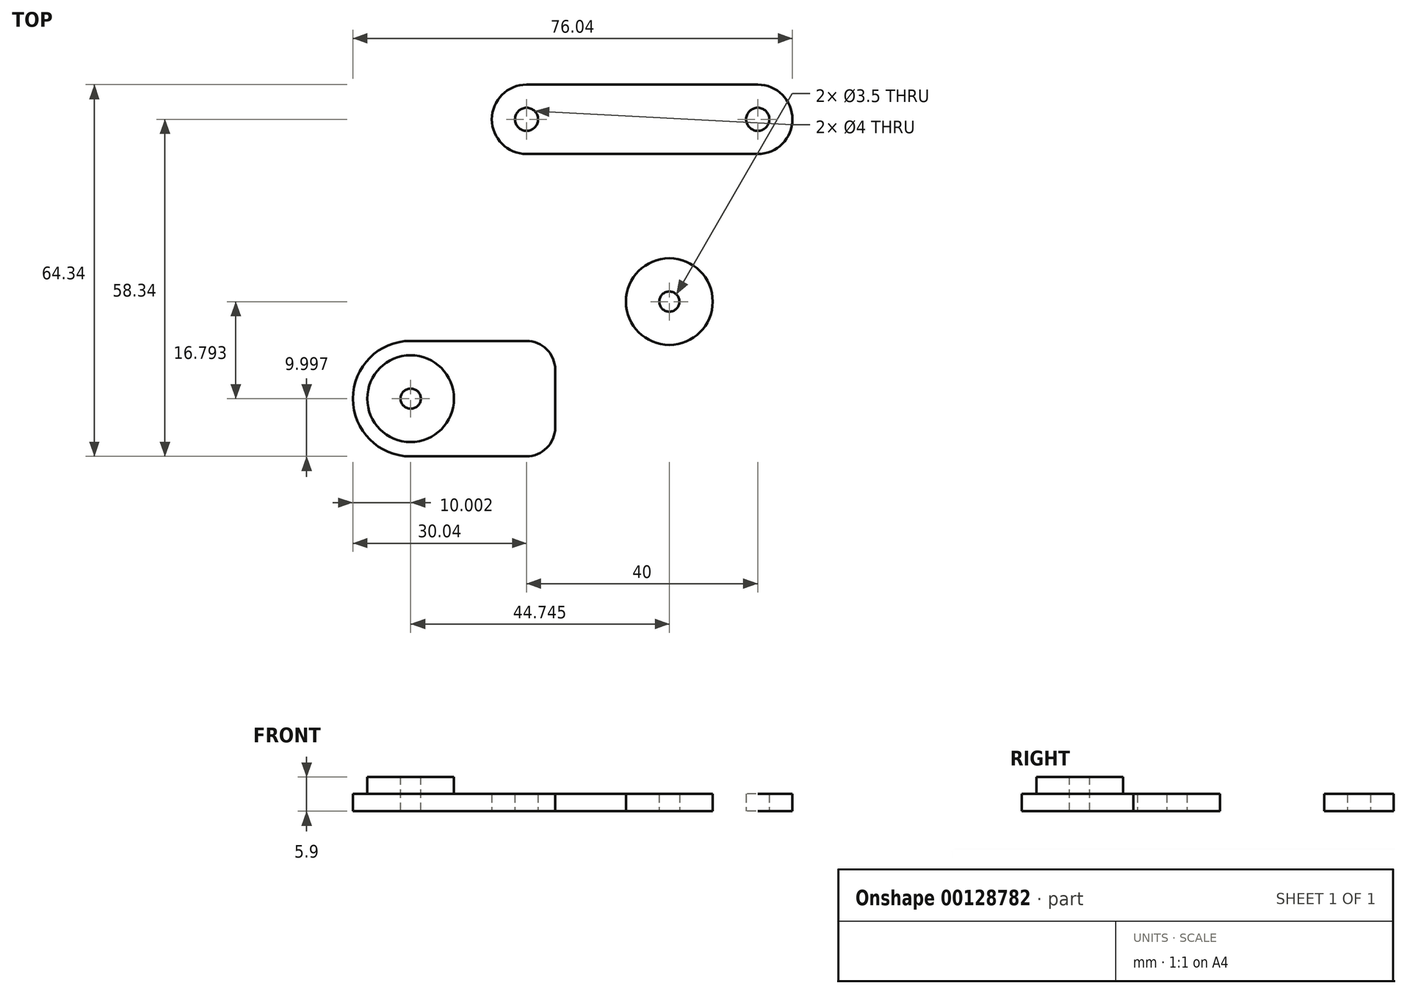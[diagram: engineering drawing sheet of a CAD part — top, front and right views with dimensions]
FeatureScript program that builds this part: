
annotation { "Feature Type Name" : "Feature", "Feature Type Description" : "" }
export const myFeature = defineFeature(function(context is Context, id is Id, definition is map)
    precondition{}
    {
        {
            var Q0;
            Q0=qCreatedBy(makeId("Top.planeOp"),FACE);
            var sketch = newSketch(context, id + "F0", { "sketchPlane" : qUnion([Q0])});
            skCircle(sketch, "E0", {"center": v(0, 0) * mm, "radius": 6 * mm});
            skCircle(sketch, "E1", {"center": v(-40, 0) * mm, "radius": 6 * mm});
            skLineSegment(sketch, "E2", {"start": v(-40, 6) * mm, "end": v(0, 6) * mm});
            skLineSegment(sketch, "E3", {"start": v(0, -6) * mm, "end": v(-40, -6) * mm});
            skCircle(sketch, "E4", {"center": v(-40, 0) * mm, "radius": 2 * mm});
            skCircle(sketch, "E5", {"center": v(0, 0) * mm, "radius": 2 * mm});
            skSolve(sketch);
        }
        {
            var Q0;
            Q0 = qSketchRegion(id + "F0", true);
            extrude(context, id + "F1", {"entities" : qUnion([Q0]), "depth" : 3 * mm});
        }
        {
            var Q0;
            Q0=qCreatedBy(makeId("Top.planeOp"),FACE);
            var sketch = newSketch(context, id + "F2", { "sketchPlane" : qUnion([Q0])});
            skLineSegment(sketch, "E6.bottom", {"start": v(-60.04, -38.34) * mm, "end": v(-35.04, -38.34) * mm});
            skLineSegment(sketch, "E6.top", {"start": v(-60.04, -58.34) * mm, "end": v(-35.04, -58.34) * mm});
            skLineSegment(sketch, "E6.right", {"start": v(-35.04, -38.34) * mm, "end": v(-35.04, -58.34) * mm});
            skArc(sketch, "E7", {"start": v(-60.04, -38.34) * mm, "mid": v(-70.04, -48.34) * mm, "end": v(-60.04, -58.34) * mm});
            skSolve(sketch);
        }
        {
            var Q0;
            Q0 = qSketchRegion(id + "F2", true);
            var Q1;
            Q1 = qConstructionFilter(qBodyType(qCreatedBy(id + "F2" ,EDGE), BodyType.WIRE), ConstructionObject.NO);
            extrude(context, id + "F3", {"entities" : qUnion([Q0]), "surfaceEntities" : qUnion([Q1]), "depth" : 3 * mm});
        }
        {
            var Q0;
            Q0=makeQuery(id+"F3.opExtrude","CAP_FACE",FACE,{"disambiguationData":[OSD([sQuery(id+"F2.wireOp",EDGE,"E6.bottom"),sQuery(id+"F2.wireOp",EDGE,"E6.top"),sQuery(id+"F2.wireOp",EDGE,"E6.right"),sQuery(id+"F2.wireOp",EDGE,"E7")])],"isStart":false});
            var sketch = newSketch(context, id + "F4", { "sketchPlane" : qUnion([Q0])});
            skCircle(sketch, "E8", {"center": v(-60.04, -48.34) * mm, "radius": 7.5 * mm});
            skSolve(sketch);
        }
        {
            var Q0;
            Q0 = qSketchRegion(id + "F4", true);
            extrude(context, id + "F5", {"entities" : qUnion([Q0]), "operationType" : NewBodyOperationType.ADD, "depth" : 2.9 * mm});
        }
        {
            var Q0;
            Q0=makeQuery(id+"F5.opExtrude","CAP_FACE",FACE,{"disambiguationData":[OSD([sQuery(id+"F4.wireOp",EDGE,"E8")])],"isStart":false});
            var sketch = newSketch(context, id + "F6", { "sketchPlane" : qUnion([Q0])});
            skCircle(sketch, "E9", {"center": v(-60.04, -48.34) * mm, "radius": 1.75 * mm});
            skSolve(sketch);
        }
        {
            var Q0;
            Q0 = qSketchRegion(id + "F6", true);
            var Q1;
            Q1=makeQuery(id+"F3.opExtrude","SWEPT_BODY",BODY,{"disambiguationData":[OSD([sQuery(id+"F2.wireOp",EDGE,"E6.bottom"),sQuery(id+"F2.wireOp",EDGE,"E6.top"),sQuery(id+"F2.wireOp",EDGE,"E6.right"),sQuery(id+"F2.wireOp",EDGE,"E7")])]});
            extrude(context, id + "F7", {"entities" : qUnion([Q0]), "operationType" : NewBodyOperationType.REMOVE, "endBound" : BoundingType.UP_TO_BODY, "oppositeDirection" : true, "endBoundEntityBody" : qUnion([Q1]), "depth" : 25 * mm});
        }
        {
            var Q0;
            Q0=qCreatedBy(makeId("Top.planeOp"),FACE);
            var sketch = newSketch(context, id + "F8", { "sketchPlane" : qUnion([Q0])});
            skCircle(sketch, "E10", {"center": v(-15.3, -31.55) * mm, "radius": 7.5 * mm});
            skCircle(sketch, "E11", {"center": v(-15.3, -31.55) * mm, "radius": 1.75 * mm});
            skSolve(sketch);
        }
        {
            var Q0;
            Q0 = qSketchRegion(id + "F8", true);
            extrude(context, id + "F9", {"entities" : qUnion([Q0]), "depth" : 3 * mm});
        }
        {
            var Q0;
            Q0=makeQuery(id+"F3.opExtrude","SWEPT_EDGE",EDGE,{"disambiguationData":[OSD([sQuery(id+"F2.wireOp",EDGE,"E6.bottom"),sQuery(id+"F2.wireOp",EDGE,"E6.right")])]});
            var Q1;
            Q1=makeQuery(id+"F3.opExtrude","SWEPT_EDGE",EDGE,{"disambiguationData":[OSD([sQuery(id+"F2.wireOp",EDGE,"E6.top"),sQuery(id+"F2.wireOp",EDGE,"E6.right")])]});
            fillet(context, id + "F10", {"entities" : qUnion([Q0, Q1]), "radius" : 5 * mm, "tangentPropagation" : true, "allowEdgeOverflow" : false});
        }
    });
